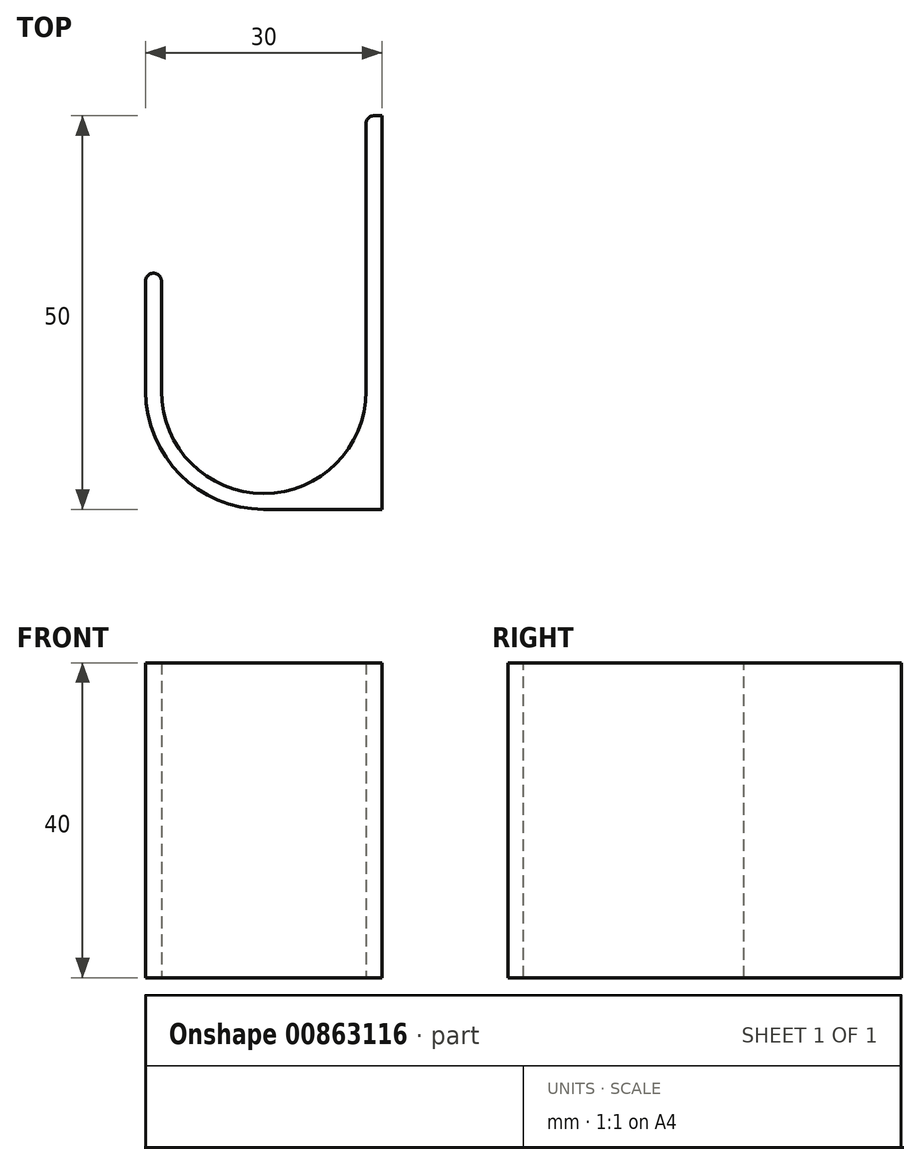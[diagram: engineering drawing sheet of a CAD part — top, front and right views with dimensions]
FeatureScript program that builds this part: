
annotation { "Feature Type Name" : "Feature", "Feature Type Description" : "" }
export const myFeature = defineFeature(function(context is Context, id is Id, definition is map)
    precondition{}
    {
        {
            var Q0;
            Q0=qCreatedBy(makeId("Top.planeOp"),FACE);
            var sketch = newSketch(context, id + "F0", { "sketchPlane" : qUnion([Q0])});
            skLineSegment(sketch, "E0.bottom", {"start": v(-26.58, 17.76) * mm, "end": v(-24.58, 17.76) * mm});
            skLineSegment(sketch, "E0.top", {"start": v(-26.58, -12.24) * mm, "end": v(-24.58, -12.24) * mm});
            skLineSegment(sketch, "E0.left", {"start": v(-26.58, 17.76) * mm, "end": v(-26.58, -12.24) * mm});
            skLineSegment(sketch, "E0.right", {"start": v(-24.58, 17.76) * mm, "end": v(-24.58, -12.24) * mm});
            skLineSegment(sketch, "E1.bottom", {"start": v(-24.58, -12.24) * mm, "end": v(1.42, -12.24) * mm});
            skLineSegment(sketch, "E1.top", {"start": v(-24.58, -10.24) * mm, "end": v(1.42, -10.24) * mm});
            skLineSegment(sketch, "E1.left", {"start": v(-24.58, -12.24) * mm, "end": v(-24.58, -10.24) * mm});
            skLineSegment(sketch, "E1.right", {"start": v(1.42, -12.24) * mm, "end": v(1.42, -10.24) * mm});
            skLineSegment(sketch, "E2.bottom", {"start": v(1.42, -12.24) * mm, "end": v(3.42, -12.24) * mm});
            skLineSegment(sketch, "E2.top", {"start": v(1.42, 37.76) * mm, "end": v(3.42, 37.76) * mm});
            skLineSegment(sketch, "E2.left", {"start": v(1.42, -12.24) * mm, "end": v(1.42, 37.76) * mm});
            skLineSegment(sketch, "E2.right", {"start": v(3.42, -12.24) * mm, "end": v(3.42, 37.76) * mm});
            skSolve(sketch);
        }
        {
            var Q0;
            Q0 = qSketchRegion(id + "F0", true);
            extrude(context, id + "F1", {"entities" : qUnion([Q0]), "depth" : 40 * mm, "offsetDistance" : 25 * mm});
        }
        {
            var Q0;
            Q0=makeQuery(id+"F1.opExtrude","SWEPT_EDGE",EDGE,{"disambiguationData":[OSD([sQuery(id+"F0.wireOp",EDGE,"E0.bottom"),sQuery(id+"F0.wireOp",EDGE,"E0.left")])]});
            var Q1;
            Q1=makeQuery(id+"F1.opExtrude","SWEPT_EDGE",EDGE,{"disambiguationData":[OSD([sQuery(id+"F0.wireOp",EDGE,"E0.bottom"),sQuery(id+"F0.wireOp",EDGE,"E0.right")])]});
            var Q2;
            Q2=makeQuery(id+"F1.opExtrude","SWEPT_EDGE",EDGE,{"disambiguationData":[OSD([sQuery(id+"F0.wireOp",EDGE,"E2.top"),sQuery(id+"F0.wireOp",EDGE,"E2.left")])]});
            fillet(context, id + "F2", {"entities" : qUnion([Q0, Q1, Q2]), "radius" : 1 * mm, "tangentPropagation" : true, "allowEdgeOverflow" : false});
        }
        {
            var Q0;
            Q0=makeQuery(id+"F1.opExtrude","SWEPT_EDGE",EDGE,{"disambiguationData":[OSD([sQuery(id+"F0.wireOp",EDGE,"E1.top"),sQuery(id+"F0.wireOp",EDGE,"E2.left")])]});
            var Q1;
            Q1=makeQuery(id+"F1.opExtrude","SWEPT_EDGE",EDGE,{"disambiguationData":[OSD([sQuery(id+"F0.wireOp",EDGE,"E0.right"),sQuery(id+"F0.wireOp",EDGE,"E1.top"),sQuery(id+"F0.wireOp",EDGE,"E1.left")])]});
            fillet(context, id + "F3", {"entities" : qUnion([Q0, Q1]), "radius" : 13 * mm, "tangentPropagation" : true, "allowEdgeOverflow" : false});
        }
        {
            var Q0;
            Q0=makeQuery(id+"F1.opExtrude","SWEPT_EDGE",EDGE,{"disambiguationData":[OSD([sQuery(id+"F0.wireOp",EDGE,"E0.top"),sQuery(id+"F0.wireOp",EDGE,"E0.left")])]});
            fillet(context, id + "F4", {"entities" : qUnion([Q0]), "radius" : 15 * mm, "tangentPropagation" : true, "allowEdgeOverflow" : false});
        }
    });
